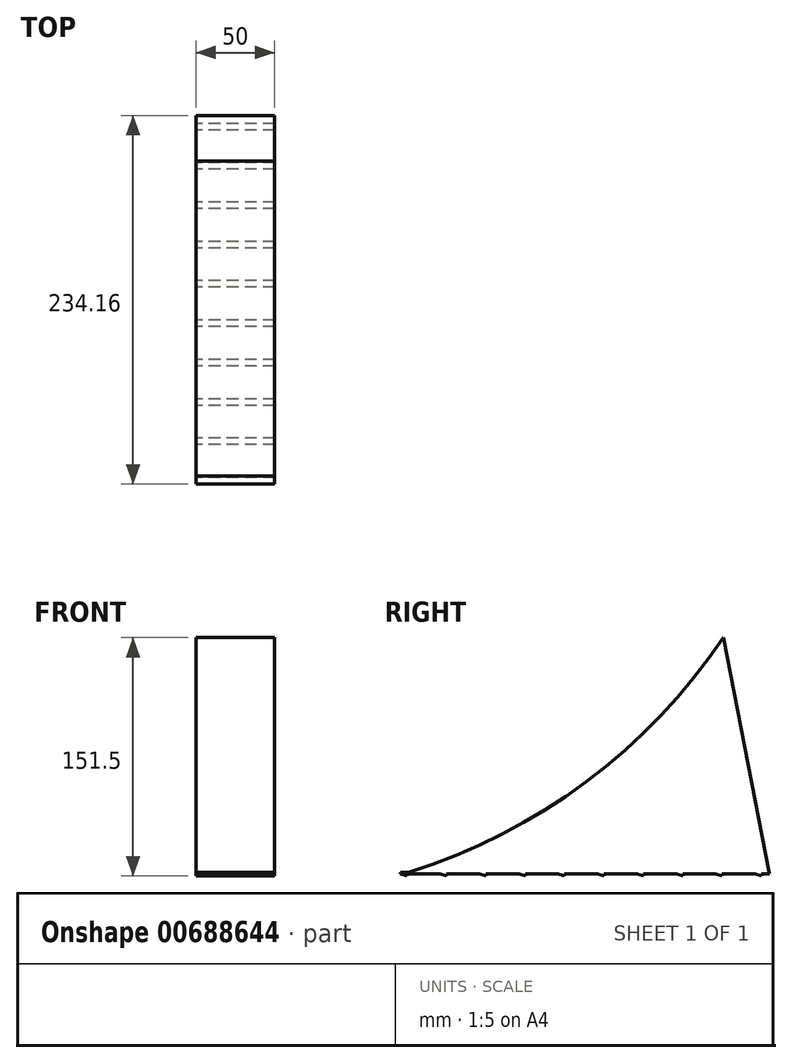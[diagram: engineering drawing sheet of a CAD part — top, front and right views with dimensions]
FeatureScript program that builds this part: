
annotation { "Feature Type Name" : "Feature", "Feature Type Description" : "" }
export const myFeature = defineFeature(function(context is Context, id is Id, definition is map)
    precondition{}
    {
        {
            var Q0;
            Q0=qCreatedBy(makeId("Right.planeOp"),FACE);
            var sketch = newSketch(context, id + "F0", { "sketchPlane" : qUnion([Q0])});
            skLineSegment(sketch, "E0.right", {"start": v(100, 75) * mm, "end": v(100, -75) * mm});
            skPoint(sketch, "E0.middle", {"position": v(0, 0) * mm});
            skLineSegment(sketch, "E1.bottom", {"start": v(-100, -75) * mm, "end": v(-105, -75) * mm});
            skLineSegment(sketch, "E1.top", {"start": v(-100, -74) * mm, "end": v(-105, -74) * mm});
            skLineSegment(sketch, "E1.left", {"start": v(-100, -75) * mm, "end": v(-100, -74) * mm});
            skLineSegment(sketch, "E1.right", {"start": v(-105, -75) * mm, "end": v(-105, -74) * mm});
            skLineSegment(sketch, "E2", {"start": v(-100, -75) * mm, "end": v(100, -75) * mm});
            skArc(sketch, "E3", {"start": v(-100, -74) * mm, "mid": v(12.75, -16.61) * mm, "end": v(100, 75) * mm});
            skLineSegment(sketch, "E4", {"start": v(100, -75) * mm, "end": v(129.16, -75) * mm});
            skLineSegment(sketch, "E5", {"start": v(129.16, -75) * mm, "end": v(100, 75) * mm});
            skLineSegment(sketch, "E6", {"start": v(-105, -75) * mm, "end": v(-100.88, -76.5) * mm});
            skLineSegment(sketch, "E7", {"start": v(-100.88, -76.5) * mm, "end": v(-100.88, -75) * mm});
            skLineSegment(sketch, "E8", {"start": v(-80, -75) * mm, "end": v(-75.88, -76.5) * mm});
            skLineSegment(sketch, "E9", {"start": v(-75.88, -76.5) * mm, "end": v(-75.88, -75) * mm});
            skLineSegment(sketch, "E10", {"start": v(-55, -75) * mm, "end": v(-50.88, -76.5) * mm});
            skLineSegment(sketch, "E11", {"start": v(-50.88, -76.5) * mm, "end": v(-50.88, -75) * mm});
            skLineSegment(sketch, "E12", {"start": v(-30, -75) * mm, "end": v(-25.88, -76.5) * mm});
            skLineSegment(sketch, "E13", {"start": v(-25.88, -76.5) * mm, "end": v(-25.88, -75) * mm});
            skLineSegment(sketch, "E14", {"start": v(-5, -75) * mm, "end": v(-0.88, -76.5) * mm});
            skLineSegment(sketch, "E15", {"start": v(-0.88, -76.5) * mm, "end": v(-0.88, -75) * mm});
            skLineSegment(sketch, "E16", {"start": v(20, -75) * mm, "end": v(24.12, -76.5) * mm});
            skLineSegment(sketch, "E17", {"start": v(24.12, -76.5) * mm, "end": v(24.12, -75) * mm});
            skLineSegment(sketch, "E18", {"start": v(45, -75) * mm, "end": v(49.12, -76.5) * mm});
            skLineSegment(sketch, "E19", {"start": v(49.12, -76.5) * mm, "end": v(49.12, -75) * mm});
            skLineSegment(sketch, "E20", {"start": v(70, -75) * mm, "end": v(74.12, -76.5) * mm});
            skLineSegment(sketch, "E21", {"start": v(74.12, -76.5) * mm, "end": v(74.12, -75) * mm});
            skLineSegment(sketch, "E22", {"start": v(95, -75) * mm, "end": v(99.12, -76.5) * mm});
            skLineSegment(sketch, "E23", {"start": v(99.12, -76.5) * mm, "end": v(99.12, -75) * mm});
            skLineSegment(sketch, "E24", {"start": v(120, -75) * mm, "end": v(124.12, -76.5) * mm});
            skLineSegment(sketch, "E25", {"start": v(124.12, -76.5) * mm, "end": v(124.12, -75) * mm});
            skLineSegment(sketch, "E26", {"start": v(145, -75) * mm, "end": v(149.12, -76.5) * mm});
            skLineSegment(sketch, "E27", {"start": v(149.12, -76.5) * mm, "end": v(149.12, -75) * mm});
            skSolve(sketch);
        }
        {
            var Q0;
            Q0=makeQuery(id+"F0.imprint","IMPRINT",FACE,{"disambiguationData":[TD([[makeQuery(id+"F0.imprint","IMPRINT",EDGE,{"derivedFrom":sQuery(id+"F0.wireOp",EDGE,"E1.bottom")}),-1.0]])]});
            var Q1;
            Q1=makeQuery(id+"F0.imprint","IMPRINT",FACE,{"disambiguationData":[TD([[makeQuery(id+"F0.imprint","IMPRINT",EDGE,{"derivedFrom":sQuery(id+"F0.wireOp",EDGE,"E0.right")}),-1.0]])]});
            var Q2;
            Q2=makeQuery(id+"F0.imprint","IMPRINT",FACE,{"disambiguationData":[TD([[makeQuery(id+"F0.imprint","IMPRINT",EDGE,{"derivedFrom":sQuery(id+"F0.wireOp",EDGE,"E0.right")}),1.0]])]});
            var Q3;
            {var subQ0=sQuery(id+"F0.wireOp",EDGE,"E6");Q3=makeQuery(id+"F0.imprint","IMPRINT",FACE,{"disambiguationData":[TD([[makeQuery(id+"F0.imprint","IMPRINT",EDGE,{"derivedFrom":subQ0}),1.0]])]});}
            var Q4;
            {var subQ0=sQuery(id+"F0.wireOp",EDGE,"E8");Q4=makeQuery(id+"F0.imprint","IMPRINT",FACE,{"disambiguationData":[TD([[makeQuery(id+"F0.imprint","IMPRINT",EDGE,{"derivedFrom":subQ0}),1.0]])]});}
            var Q5;
            {var subQ0=sQuery(id+"F0.wireOp",EDGE,"E10");Q5=makeQuery(id+"F0.imprint","IMPRINT",FACE,{"disambiguationData":[TD([[makeQuery(id+"F0.imprint","IMPRINT",EDGE,{"derivedFrom":subQ0}),1.0]])]});}
            var Q6;
            {var subQ0=sQuery(id+"F0.wireOp",EDGE,"E12");Q6=makeQuery(id+"F0.imprint","IMPRINT",FACE,{"disambiguationData":[TD([[makeQuery(id+"F0.imprint","IMPRINT",EDGE,{"derivedFrom":subQ0}),1.0]])]});}
            var Q7;
            {var subQ0=sQuery(id+"F0.wireOp",EDGE,"E14");Q7=makeQuery(id+"F0.imprint","IMPRINT",FACE,{"disambiguationData":[TD([[makeQuery(id+"F0.imprint","IMPRINT",EDGE,{"derivedFrom":subQ0}),1.0]])]});}
            var Q8;
            {var subQ0=sQuery(id+"F0.wireOp",EDGE,"E16");Q8=makeQuery(id+"F0.imprint","IMPRINT",FACE,{"disambiguationData":[TD([[makeQuery(id+"F0.imprint","IMPRINT",EDGE,{"derivedFrom":subQ0}),1.0]])]});}
            var Q9;
            {var subQ0=sQuery(id+"F0.wireOp",EDGE,"E18");Q9=makeQuery(id+"F0.imprint","IMPRINT",FACE,{"disambiguationData":[TD([[makeQuery(id+"F0.imprint","IMPRINT",EDGE,{"derivedFrom":subQ0}),1.0]])]});}
            var Q10;
            {var subQ0=sQuery(id+"F0.wireOp",EDGE,"E20");Q10=makeQuery(id+"F0.imprint","IMPRINT",FACE,{"disambiguationData":[TD([[makeQuery(id+"F0.imprint","IMPRINT",EDGE,{"derivedFrom":subQ0}),1.0]])]});}
            var Q11;
            {var subQ0=sQuery(id+"F0.wireOp",EDGE,"E22");Q11=makeQuery(id+"F0.imprint","IMPRINT",FACE,{"disambiguationData":[TD([[makeQuery(id+"F0.imprint","IMPRINT",EDGE,{"derivedFrom":subQ0}),1.0]])]});}
            var Q12;
            {var subQ0=sQuery(id+"F0.wireOp",EDGE,"E24");Q12=makeQuery(id+"F0.imprint","IMPRINT",FACE,{"disambiguationData":[TD([[makeQuery(id+"F0.imprint","IMPRINT",EDGE,{"derivedFrom":subQ0}),1.0]])]});}
            var Q13;
            {var subQ0=sQuery(id+"F0.wireOp",EDGE,"E26");Q13=makeQuery(id+"F0.imprint","IMPRINT",FACE,{"disambiguationData":[TD([[makeQuery(id+"F0.imprint","IMPRINT",EDGE,{"derivedFrom":subQ0}),1.0]])]});}
            extrude(context, id + "F1", {"entities" : qUnion([Q0, Q1, Q2, Q3, Q4, Q5, Q6, Q7, Q8, Q9, Q10, Q11, Q12, Q13]), "endBound" : BoundingType.SYMMETRIC, "depth" : 50 * mm, "offsetDistance" : 25 * mm});
        }
    });
